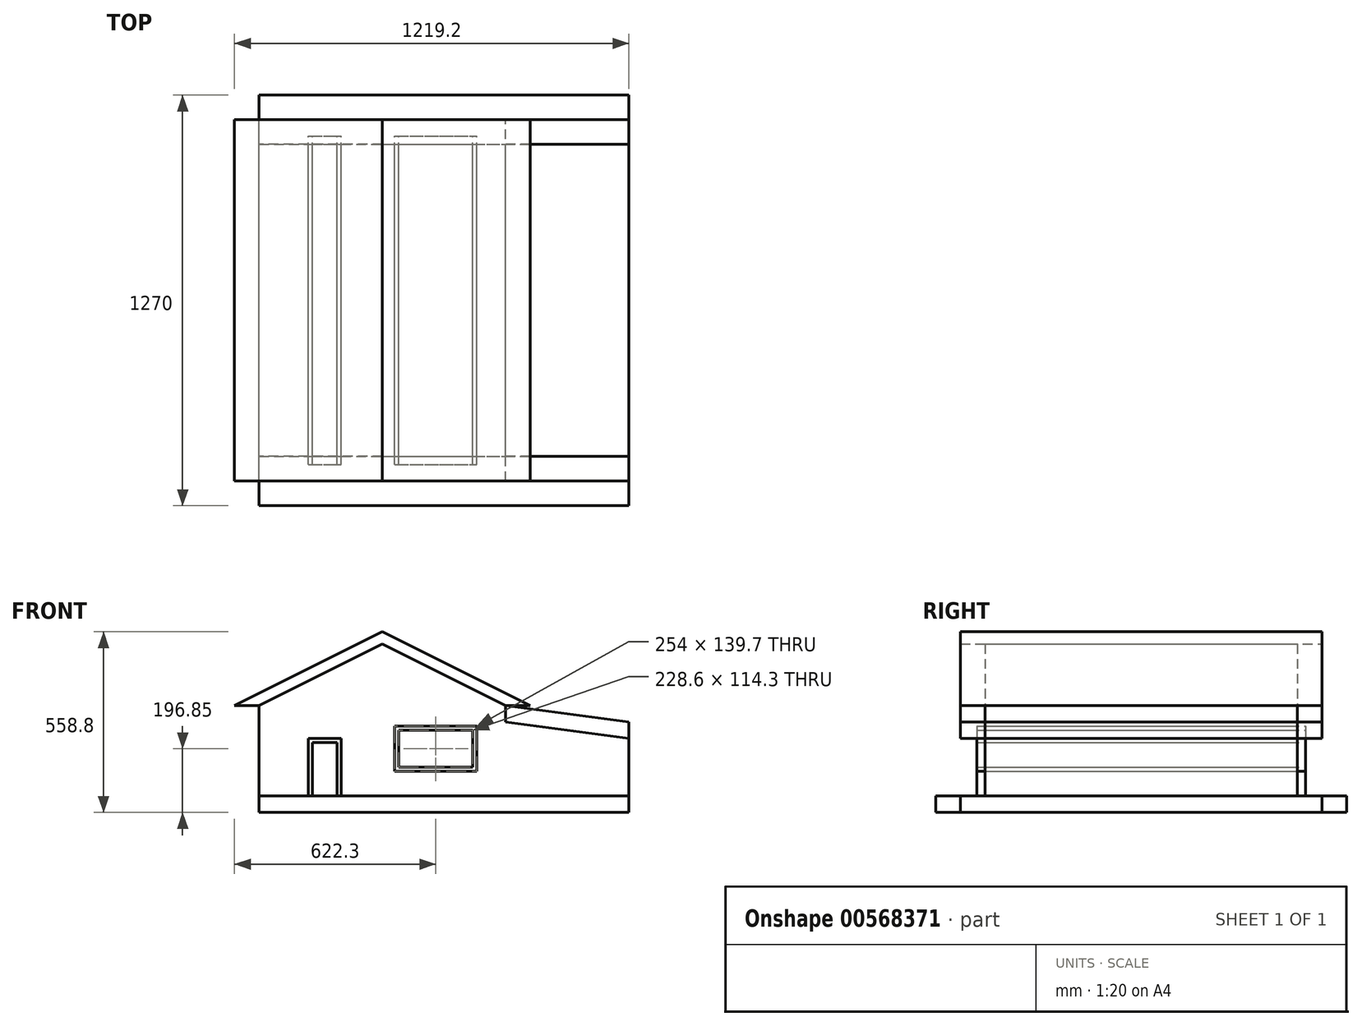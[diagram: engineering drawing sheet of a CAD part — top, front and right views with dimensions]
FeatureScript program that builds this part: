
annotation { "Feature Type Name" : "Feature", "Feature Type Description" : "" }
export const myFeature = defineFeature(function(context is Context, id is Id, definition is map)
    precondition{}
    {
        {
            var Q0;
            Q0=qCreatedBy(makeId("Front.planeOp"),FACE);
            var sketch = newSketch(context, id + "F0", { "sketchPlane" : qUnion([Q0])});
            skLineSegment(sketch, "E0", {"start": v(0, 0) * mm, "end": v(-381, 0) * mm});
            skLineSegment(sketch, "E1", {"start": v(0, 0) * mm, "end": v(381, 0) * mm});
            skLineSegment(sketch, "E2", {"start": v(-381, 0) * mm, "end": v(-381, -279.4) * mm});
            skLineSegment(sketch, "E3", {"start": v(0, 0) * mm, "end": v(0, 190.5) * mm});
            skLineSegment(sketch, "E4", {"start": v(0, 190.5) * mm, "end": v(381, 0) * mm});
            skLineSegment(sketch, "E5", {"start": v(0, 190.5) * mm, "end": v(-381, 0) * mm});
            skLineSegment(sketch, "E6", {"start": v(381, 0) * mm, "end": v(381, -279.4) * mm});
            skLineSegment(sketch, "E7", {"start": v(-381, -279.4) * mm, "end": v(381, -279.4) * mm});
            skLineSegment(sketch, "E8", {"start": v(-381, -279.4) * mm, "end": v(-381, -330.2) * mm});
            skLineSegment(sketch, "E9", {"start": v(381, -279.4) * mm, "end": v(381, -330.2) * mm});
            skLineSegment(sketch, "E10", {"start": v(381, -330.2) * mm, "end": v(-381, -330.2) * mm});
            skLineSegment(sketch, "E11", {"start": v(381, -330.2) * mm, "end": v(762, -330.2) * mm});
            skLineSegment(sketch, "E12", {"start": v(762, -330.2) * mm, "end": v(762, -279.4) * mm});
            skLineSegment(sketch, "E13", {"start": v(381, -279.4) * mm, "end": v(762, -279.4) * mm});
            skLineSegment(sketch, "E14", {"start": v(762, -279.4) * mm, "end": v(762, -50.8) * mm});
            skLineSegment(sketch, "E15", {"start": v(762, -50.8) * mm, "end": v(381, 0) * mm});
            skLineSegment(sketch, "E16", {"start": v(0, 190.5) * mm, "end": v(0, 228.6) * mm});
            skLineSegment(sketch, "E17", {"start": v(381, 0) * mm, "end": v(457.2, 0) * mm});
            skLineSegment(sketch, "E18", {"start": v(457.2, 0) * mm, "end": v(0, 228.6) * mm});
            skLineSegment(sketch, "E19", {"start": v(-381, 0) * mm, "end": v(-457.2, 0) * mm});
            skLineSegment(sketch, "E20", {"start": v(-457.2, 0) * mm, "end": v(0, 228.6) * mm});
            skLineSegment(sketch, "E21", {"start": v(381, 0) * mm, "end": v(381, -50.8) * mm});
            skLineSegment(sketch, "E22", {"start": v(381, -50.8) * mm, "end": v(762, -101.65) * mm});
            skLineSegment(sketch, "E23", {"start": v(50.8, -76.2) * mm, "end": v(50.8, -190.5) * mm});
            skLineSegment(sketch, "E24", {"start": v(50.8, -76.2) * mm, "end": v(279.4, -76.2) * mm});
            skLineSegment(sketch, "E25", {"start": v(279.4, -76.2) * mm, "end": v(279.4, -190.5) * mm});
            skLineSegment(sketch, "E26", {"start": v(50.8, -190.5) * mm, "end": v(279.4, -190.5) * mm});
            skLineSegment(sketch, "E27", {"start": v(-228.6, -279.4) * mm, "end": v(-228.6, -101.6) * mm});
            skLineSegment(sketch, "E28", {"start": v(-228.6, -101.6) * mm, "end": v(-127, -101.6) * mm});
            skLineSegment(sketch, "E29", {"start": v(-127, -101.6) * mm, "end": v(-127, -279.4) * mm});
            skLineSegment(sketch, "E30", {"start": v(-215.9, -279.4) * mm, "end": v(-215.9, -114.3) * mm});
            skLineSegment(sketch, "E31", {"start": v(-215.9, -114.3) * mm, "end": v(-139.7, -114.3) * mm});
            skLineSegment(sketch, "E32", {"start": v(-139.7, -114.3) * mm, "end": v(-139.7, -279.4) * mm});
            skLineSegment(sketch, "E33.bottom", {"start": v(38.1, -63.5) * mm, "end": v(292.1, -63.5) * mm});
            skLineSegment(sketch, "E33.top", {"start": v(38.1, -203.2) * mm, "end": v(292.1, -203.2) * mm});
            skLineSegment(sketch, "E33.left", {"start": v(38.1, -63.5) * mm, "end": v(38.1, -203.2) * mm});
            skLineSegment(sketch, "E33.right", {"start": v(292.1, -63.5) * mm, "end": v(292.1, -203.2) * mm});
            skSolve(sketch);
        }
        {
            var Q0;
            Q0=makeQuery(id+"F0.imprint","IMPRINT",FACE,{"disambiguationData":[TD([[makeQuery(id+"F0.imprint","IMPRINT",EDGE,{"derivedFrom":sQuery(id+"F0.wireOp",EDGE,"E0")}),-1.0]])]});
            var Q1;
            Q1=makeQuery(id+"F0.imprint","IMPRINT",FACE,{"disambiguationData":[TD([[makeQuery(id+"F0.imprint","IMPRINT",EDGE,{"derivedFrom":sQuery(id+"F0.wireOp",EDGE,"E1")}),1.0]])]});
            var Q2;
            Q2=makeQuery(id+"F0.imprint","IMPRINT",FACE,{"disambiguationData":[TD([[makeQuery(id+"F0.imprint","IMPRINT",EDGE,{"derivedFrom":sQuery(id+"F0.wireOp",EDGE,"E0")}),1.0]])]});
            var Q3;
            Q3=makeQuery(id+"F0.imprint","IMPRINT",FACE,{"disambiguationData":[TD([[makeQuery(id+"F0.imprint","IMPRINT",EDGE,{"derivedFrom":sQuery(id+"F0.wireOp",EDGE,"E6")}),1.0]])]});
            var Q4;
            {var subQ0=sQuery(id+"F0.wireOp",EDGE,"E30");Q4=makeQuery(id+"F0.imprint","IMPRINT",FACE,{"disambiguationData":[TD([[makeQuery(id+"F0.imprint","IMPRINT",EDGE,{"derivedFrom":subQ0}),-1.0]])]});}
            var Q5;
            Q5=makeQuery(id+"F0.imprint","IMPRINT",FACE,{"disambiguationData":[TD([[makeQuery(id+"F0.imprint","IMPRINT",EDGE,{"derivedFrom":sQuery(id+"F0.wireOp",EDGE,"E23")}),1.0]])]});
            extrude(context, id + "F1", {"entities" : qUnion([Q0, Q1, Q2, Q3, Q4, Q5]), "endBound" : BoundingType.SYMMETRIC, "depth" : 965.2 * mm, "offsetDistance" : 25.4 * mm});
        }
        {
            var Q0;
            {var subQ0=sQuery(id+"F0.wireOp",EDGE,"E27");Q0=makeQuery(id+"F0.imprint","IMPRINT",FACE,{"disambiguationData":[TD([[makeQuery(id+"F0.imprint","IMPRINT",EDGE,{"derivedFrom":subQ0}),-1.0]])]});}
            var Q1;
            Q1=makeQuery(id+"F0.imprint","IMPRINT",FACE,{"disambiguationData":[TD([[makeQuery(id+"F0.imprint","IMPRINT",EDGE,{"derivedFrom":sQuery(id+"F0.wireOp",EDGE,"E23")}),-1.0]])]});
            extrude(context, id + "F2", {"entities" : qUnion([Q0, Q1]), "endBound" : BoundingType.SYMMETRIC, "depth" : 1016 * mm, "offsetDistance" : 25.4 * mm});
        }
        {
            var Q0;
            Q0=makeQuery(id+"F0.imprint","IMPRINT",FACE,{"disambiguationData":[TD([[makeQuery(id+"F0.imprint","IMPRINT",EDGE,{"derivedFrom":sQuery(id+"F0.wireOp",EDGE,"E5")}),-1.0]])]});
            var Q1;
            {var subQ0=sQuery(id+"F0.wireOp",EDGE,"E15");Q1=makeQuery(id+"F0.imprint","IMPRINT",FACE,{"disambiguationData":[TD([[makeQuery(id+"F0.imprint","IMPRINT",EDGE,{"derivedFrom":subQ0}),1.0]])]});}
            var Q2;
            Q2=makeQuery(id+"F0.imprint","IMPRINT",FACE,{"disambiguationData":[TD([[makeQuery(id+"F0.imprint","IMPRINT",EDGE,{"derivedFrom":sQuery(id+"F0.wireOp",EDGE,"E9")}),1.0]])]});
            var Q3;
            {var subQ5=sQuery(id+"F0.wireOp",EDGE,"E8");Q3=makeQuery(id+"F0.imprint","IMPRINT",FACE,{"disambiguationData":[TD([[makeQuery(id+"F0.imprint","IMPRINT",EDGE,{"derivedFrom":subQ5}),1.0]])]});}
            var Q4;
            Q4=makeQuery(id+"F0.imprint","IMPRINT",FACE,{"disambiguationData":[TD([[makeQuery(id+"F0.imprint","IMPRINT",EDGE,{"derivedFrom":sQuery(id+"F0.wireOp",EDGE,"E4")}),1.0]])]});
            extrude(context, id + "F3", {"entities" : qUnion([Q0, Q1, Q2, Q3, Q4]), "endBound" : BoundingType.SYMMETRIC, "depth" : 1117.6 * mm, "offsetDistance" : 25.4 * mm});
        }
        {
            var Q0;
            {var subQ5=sQuery(id+"F0.wireOp",EDGE,"E8");Q0=makeQuery(id+"F0.imprint","IMPRINT",FACE,{"disambiguationData":[TD([[makeQuery(id+"F0.imprint","IMPRINT",EDGE,{"derivedFrom":subQ5}),1.0]])]});}
            var Q1;
            Q1=makeQuery(id+"F0.imprint","IMPRINT",FACE,{"disambiguationData":[TD([[makeQuery(id+"F0.imprint","IMPRINT",EDGE,{"derivedFrom":sQuery(id+"F0.wireOp",EDGE,"E9")}),1.0]])]});
            extrude(context, id + "F4", {"entities" : qUnion([Q0, Q1]), "endBound" : BoundingType.SYMMETRIC, "depth" : 1270 * mm, "offsetDistance" : 25.4 * mm});
        }
    });
